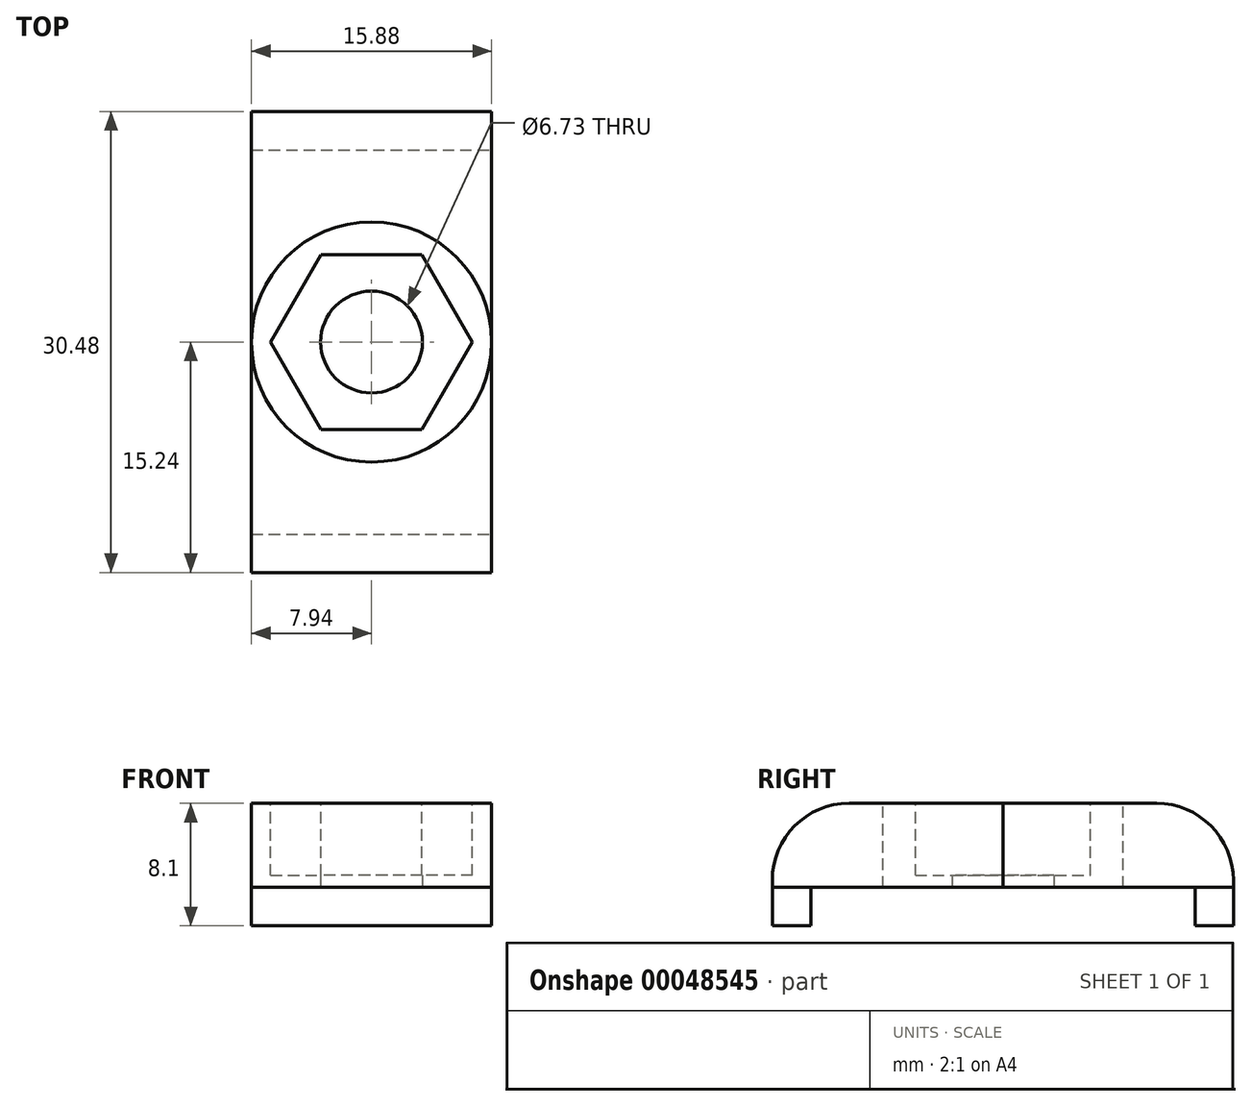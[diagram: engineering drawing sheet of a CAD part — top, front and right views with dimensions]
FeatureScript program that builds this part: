
annotation { "Feature Type Name" : "Feature", "Feature Type Description" : "" }
export const myFeature = defineFeature(function(context is Context, id is Id, definition is map)
    precondition{}
    {
        {
            var Q0;
            Q0=qCreatedBy(makeId("Top.planeOp"),FACE);
            var sketch = newSketch(context, id + "F0", { "sketchPlane" : qUnion([Q0])});
            skCircle(sketch, "E0", {"center": v(0, 0) * mm, "radius": 7.94 * mm});
            skCircle(sketch, "E1", {"center": v(0, 0) * mm, "radius": 3.37 * mm});
            skSolve(sketch);
        }
        {
            var Q0;
            Q0=makeQuery(id+"F0.imprint","IMPRINT",FACE,{"disambiguationData":[TD([[makeQuery(id+"F0.imprint","IMPRINT",EDGE,{"derivedFrom":sQuery(id+"F0.wireOp",EDGE,"E0")}),1.0]])]});
            extrude(context, id + "F1", {"entities" : qUnion([Q0]), "depth" : 5.56 * mm});
        }
        {
            var Q0;
            Q0=makeQuery(id+"F1.opExtrude","CAP_FACE",FACE,{"disambiguationData":[OSD([sQuery(id+"F0.wireOp",EDGE,"E0"),sQuery(id+"F0.wireOp",EDGE,"E1")])],"isStart":false});
            var sketch = newSketch(context, id + "F2", { "sketchPlane" : qUnion([Q0])});
            skCircle(sketch, "E2.cCircle", {"center": v(0, 0) * mm, "radius": 6.67 * mm, "construction": true});
            skLineSegment(sketch, "E2.0", {"start": v(-6.67, 0) * mm, "end": v(-3.34, 5.78) * mm});
            skLineSegment(sketch, "E2.1", {"start": v(-3.34, 5.78) * mm, "end": v(3.34, 5.78) * mm});
            skLineSegment(sketch, "E2.2", {"start": v(3.34, 5.78) * mm, "end": v(6.67, 0) * mm});
            skLineSegment(sketch, "E2.3", {"start": v(6.67, 0) * mm, "end": v(3.34, -5.78) * mm});
            skLineSegment(sketch, "E2.4", {"start": v(3.34, -5.78) * mm, "end": v(-3.34, -5.78) * mm});
            skLineSegment(sketch, "E2.5", {"start": v(-3.34, -5.78) * mm, "end": v(-6.67, 0) * mm});
            skSolve(sketch);
        }
        {
            var Q0;
            Q0=makeQuery(id+"F2.imprint","IMPRINT",FACE,{"disambiguationData":[TD([[makeQuery(id+"F2.imprint","IMPRINT",EDGE,{"derivedFrom":sQuery(id+"F2.wireOp",EDGE,"E2.0")}),-1.0]])]});
            extrude(context, id + "F3", {"entities" : qUnion([Q0]), "operationType" : NewBodyOperationType.REMOVE, "oppositeDirection" : true, "depth" : 4.76 * mm});
        }
        {
            var Q0;
            Q0=makeQuery(id+"F1.opExtrude","CAP_FACE",FACE,{"disambiguationData":[OSD([sQuery(id+"F0.wireOp",EDGE,"E0"),sQuery(id+"F0.wireOp",EDGE,"E1")])],"isStart":false});
            var sketch = newSketch(context, id + "F4", { "sketchPlane" : qUnion([Q0])});
            skLineSegment(sketch, "E3.rect.bottom", {"start": v(-7.94, 15.24) * mm, "end": v(7.94, 15.24) * mm});
            skLineSegment(sketch, "E3.rect.top", {"start": v(-7.94, -15.24) * mm, "end": v(7.94, -15.24) * mm});
            skLineSegment(sketch, "E3.rect.left", {"start": v(-7.94, 15.24) * mm, "end": v(-7.94, -15.24) * mm});
            skLineSegment(sketch, "E3.rect.right", {"start": v(7.94, 15.24) * mm, "end": v(7.94, -15.24) * mm});
            skPoint(sketch, "E3.rect.middle", {"position": v(0, 0) * mm});
            skSolve(sketch);
        }
        {
            var Q0;
            {var subQ0=sQuery(id+"F4.wireOp",EDGE,"E3.rect.bottom");Q0=makeQuery(id+"F4.imprint","IMPRINT",FACE,{"disambiguationData":[TD([[makeQuery(id+"F4.imprint","IMPRINT",EDGE,{"derivedFrom":subQ0}),-1.0]])]});}
            var Q1;
            {var subQ0=sQuery(id+"F4.wireOp",EDGE,"E3.rect.top");Q1=makeQuery(id+"F4.imprint","IMPRINT",FACE,{"disambiguationData":[TD([[makeQuery(id+"F4.imprint","IMPRINT",EDGE,{"derivedFrom":subQ0}),1.0]])]});}
            extrude(context, id + "F5", {"entities" : qUnion([Q0, Q1]), "oppositeDirection" : true, "depth" : 5.56 * mm});
        }
        {
            var Q0;
            Q0=makeQuery(id+"F5.opExtrude","CAP_FACE",FACE,{"disambiguationData":[OSD([sQuery(id+"F0.wireOp",EDGE,"E0"),sQuery(id+"F4.wireOp",EDGE,"E3.rect.top"),sQuery(id+"F4.wireOp",EDGE,"E3.rect.left"),sQuery(id+"F4.wireOp",EDGE,"E3.rect.right")])],"isStart":false});
            var sketch = newSketch(context, id + "F6", { "sketchPlane" : qUnion([Q0])});
            skLineSegment(sketch, "E4.bottom", {"start": v(-7.94, 15.24) * mm, "end": v(7.94, 15.24) * mm});
            skLineSegment(sketch, "E4.top", {"start": v(-7.94, 12.7) * mm, "end": v(7.94, 12.7) * mm});
            skLineSegment(sketch, "E4.left", {"start": v(-7.94, 15.24) * mm, "end": v(-7.94, 12.7) * mm});
            skLineSegment(sketch, "E4.right", {"start": v(7.94, 15.24) * mm, "end": v(7.94, 12.7) * mm});
            skSolve(sketch);
        }
        {
            var Q0;
            Q0=makeQuery(id+"F5.opExtrude","CAP_FACE",FACE,{"disambiguationData":[OSD([sQuery(id+"F0.wireOp",EDGE,"E0"),sQuery(id+"F4.wireOp",EDGE,"E3.rect.bottom"),sQuery(id+"F4.wireOp",EDGE,"E3.rect.left"),sQuery(id+"F4.wireOp",EDGE,"E3.rect.right")])],"isStart":false});
            var sketch = newSketch(context, id + "F7", { "sketchPlane" : qUnion([Q0])});
            skLineSegment(sketch, "E5.bottom", {"start": v(-7.94, -15.24) * mm, "end": v(7.94, -15.24) * mm});
            skLineSegment(sketch, "E5.top", {"start": v(-7.94, -12.7) * mm, "end": v(7.94, -12.7) * mm});
            skLineSegment(sketch, "E5.left", {"start": v(-7.94, -15.24) * mm, "end": v(-7.94, -12.7) * mm});
            skLineSegment(sketch, "E5.right", {"start": v(7.94, -15.24) * mm, "end": v(7.94, -12.7) * mm});
            skSolve(sketch);
        }
        {
            var Q0;
            Q0=makeQuery(id+"F6.imprint","IMPRINT",FACE,{"disambiguationData":[TD([[makeQuery(id+"F6.imprint","IMPRINT",EDGE,{"derivedFrom":sQuery(id+"F6.wireOp",EDGE,"E4.bottom")}),-1.0]])]});
            var Q1;
            Q1=makeQuery(id+"F7.imprint","IMPRINT",FACE,{"disambiguationData":[TD([[makeQuery(id+"F7.imprint","IMPRINT",EDGE,{"derivedFrom":sQuery(id+"F7.wireOp",EDGE,"E5.bottom")}),1.0]])]});
            extrude(context, id + "F8", {"entities" : qUnion([Q0, Q1]), "depth" : 2.54 * mm});
        }
        {
            var Q0;
            Q0=makeQuery(id+"F5.opExtrude","CAP_EDGE",EDGE,{"disambiguationData":[OSD([sQuery(id+"F4.wireOp",EDGE,"E3.rect.top")])],"isStart":true});
            var Q1;
            Q1=makeQuery(id+"F5.opExtrude","CAP_EDGE",EDGE,{"disambiguationData":[OSD([sQuery(id+"F4.wireOp",EDGE,"E3.rect.bottom")])],"isStart":true});
            fillet(context, id + "F9", {"entities" : qUnion([Q0, Q1]), "radius" : 5.08 * mm, "tangentPropagation" : true, "allowEdgeOverflow" : false});
        }
    });
